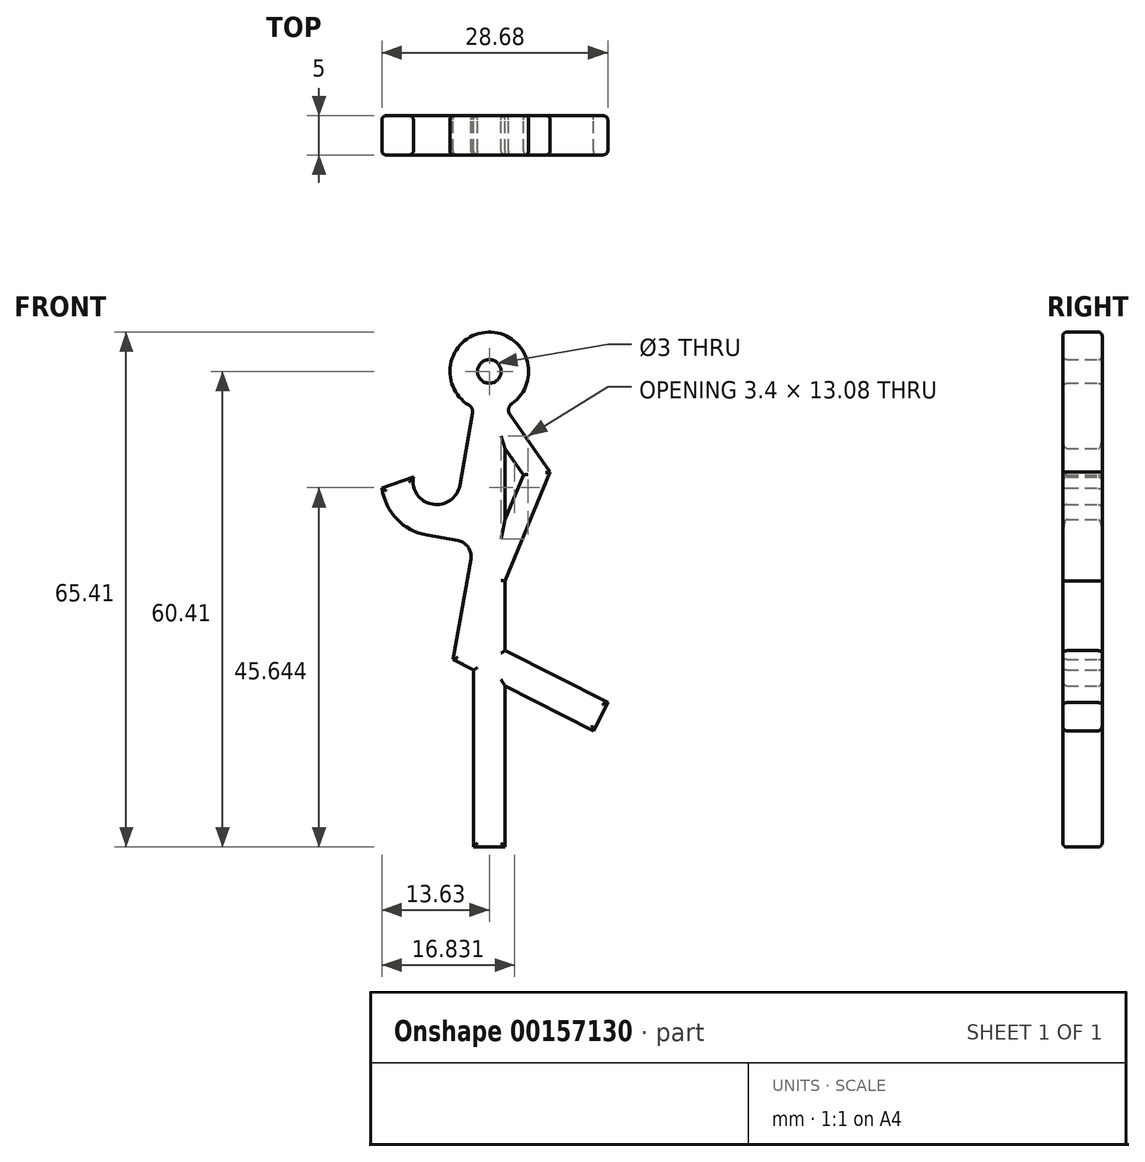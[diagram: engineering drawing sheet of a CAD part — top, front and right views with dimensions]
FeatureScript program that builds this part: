
annotation { "Feature Type Name" : "Feature", "Feature Type Description" : "" }
export const myFeature = defineFeature(function(context is Context, id is Id, definition is map)
    precondition{}
    {
        {
            var Q0;
            Q0=qCreatedBy(makeId("Front.planeOp"),FACE);
            var sketch = newSketch(context, id + "F0", { "sketchPlane" : qUnion([Q0])});
            skCircle(sketch, "E0", {"center": v(0, 0) * mm, "radius": 1.5 * mm});
            skCircle(sketch, "E1", {"center": v(0, 0) * mm, "radius": 5 * mm});
            skLineSegment(sketch, "E2", {"start": v(2, -4.58) * mm, "end": v(2, -60.41) * mm});
            skLineSegment(sketch, "E3", {"start": v(2, -60.41) * mm, "end": v(-2, -60.41) * mm});
            skLineSegment(sketch, "E4", {"start": v(-2, -60.41) * mm, "end": v(-2, -4.58) * mm});
            skLineSegment(sketch, "E5", {"start": v(2, -4.58) * mm, "end": v(7.74, -12.77) * mm});
            skLineSegment(sketch, "E6", {"start": v(7.74, -12.77) * mm, "end": v(2, -26.63) * mm});
            skLineSegment(sketch, "E7.0", {"start": v(4.33, -13.15) * mm, "end": v(-0.77, -25.49) * mm});
            skLineSegment(sketch, "E7.1", {"start": v(-0.46, -6.3) * mm, "end": v(4.33, -13.15) * mm});
            skLineSegment(sketch, "E8", {"start": v(-2, -4.58) * mm, "end": v(-3.74, -14.43) * mm});
            skLineSegment(sketch, "E9.0", {"start": v(-2, -21.84) * mm, "end": v(-7.9, -20.8) * mm});
            skArc(sketch, "E10", {"start": v(-3.74, -14.43) * mm, "mid": v(-7.21, -16.86) * mm, "end": v(-9.65, -13.39) * mm});
            skArc(sketch, "E11.0", {"start": v(-7.9, -20.8) * mm, "mid": v(-12.42, -17.92) * mm, "end": v(-13.58, -12.7) * mm});
            skLineSegment(sketch, "E12", {"start": v(-9.65, -13.39) * mm, "end": v(-13.63, -14.84) * mm});
            skLineSegment(sketch, "E13", {"start": v(-2, -21.84) * mm, "end": v(-4.6, -36.62) * mm});
            skLineSegment(sketch, "E14", {"start": v(-4.6, -36.62) * mm, "end": v(13.24, -45.65) * mm});
            skLineSegment(sketch, "E15.0", {"start": v(-0.15, -34.39) * mm, "end": v(15.05, -42.08) * mm});
            skLineSegment(sketch, "E15.1", {"start": v(1.94, -22.54) * mm, "end": v(-0.15, -34.39) * mm});
            skLineSegment(sketch, "E16", {"start": v(15.05, -42.08) * mm, "end": v(13.24, -45.65) * mm});
            skSolve(sketch);
        }
        {
            var Q0;
            Q0=makeQuery(id+"F0.imprint","IMPRINT",FACE,{"disambiguationData":[TD([[makeQuery(id+"F0.imprint","IMPRINT",EDGE,{"derivedFrom":sQuery(id+"F0.wireOp",EDGE,"E0")}),-1.0]])]});
            var Q1;
            {var subQ1=sQuery(id+"F0.wireOp",EDGE,"E5");Q1=makeQuery(id+"F0.imprint","IMPRINT",FACE,{"disambiguationData":[TD([[makeQuery(id+"F0.imprint","IMPRINT",EDGE,{"derivedFrom":subQ1}),-1.0]])]});}
            var Q2;
            {var subQ0=sQuery(id+"F0.wireOp",EDGE,"E2");var subQ7=makeQuery(id+"F0.imprint","INTERSECT",VERTEX,{"derivedFrom":[subQ0,sQuery(id+"F0.wireOp",EDGE,"E7.1")]});Q2=makeQuery(id+"F0.imprint","IMPRINT",FACE,{"disambiguationData":[TD([[makeQuery(id+"F0.imprint","IMPRINT",EDGE,{"disambiguationData":[TD([[subQ7,-1.0]])],"derivedFrom":subQ0}),-1.0]])]});}
            var Q3;
            {var subQ1=sQuery(id+"F0.wireOp",EDGE,"E8");Q3=makeQuery(id+"F0.imprint","IMPRINT",FACE,{"disambiguationData":[TD([[makeQuery(id+"F0.imprint","IMPRINT",EDGE,{"derivedFrom":subQ1}),1.0]])]});}
            var Q4;
            {var subQ0=sQuery(id+"F0.wireOp",EDGE,"E13");Q4=makeQuery(id+"F0.imprint","IMPRINT",FACE,{"disambiguationData":[TD([[makeQuery(id+"F0.imprint","IMPRINT",EDGE,{"derivedFrom":subQ0}),1.0]])]});}
            var Q5;
            {var subQ5=sQuery(id+"F0.wireOp",EDGE,"E16");Q5=makeQuery(id+"F0.imprint","IMPRINT",FACE,{"disambiguationData":[TD([[makeQuery(id+"F0.imprint","IMPRINT",EDGE,{"derivedFrom":subQ5}),-1.0]])]});}
            var Q6;
            {var subQ0=sQuery(id+"F0.wireOp",EDGE,"E3");Q6=makeQuery(id+"F0.imprint","IMPRINT",FACE,{"disambiguationData":[TD([[makeQuery(id+"F0.imprint","IMPRINT",EDGE,{"derivedFrom":subQ0}),-1.0]])]});}
            extrude(context, id + "F1", {"entities" : qUnion([Q0, Q1, Q2, Q3, Q4, Q5, Q6]), "depth" : 5 * mm});
        }
        {
            var Q0;
            Q0=makeQuery(id+"F1.opExtrude","SWEPT_EDGE",EDGE,{"disambiguationData":[OSD([sQuery(id+"F0.wireOp",EDGE,"E4"),sQuery(id+"F0.wireOp",EDGE,"E9.0"),sQuery(id+"F0.wireOp",EDGE,"E13")])]});
            fillet(context, id + "F2", {"entities" : qUnion([Q0]), "radius" : 2 * mm, "tangentPropagation" : true, "allowEdgeOverflow" : false});
        }
        {
            var Q0;
            Q0=makeQuery(id+"F1.opExtrude","SWEPT_EDGE",EDGE,{"disambiguationData":[OSD([sQuery(id+"F0.wireOp",EDGE,"E1"),sQuery(id+"F0.wireOp",EDGE,"E4"),sQuery(id+"F0.wireOp",EDGE,"E8")])]});
            var Q1;
            Q1=makeQuery(id+"F1.opExtrude","SWEPT_EDGE",EDGE,{"disambiguationData":[OSD([sQuery(id+"F0.wireOp",EDGE,"E1"),sQuery(id+"F0.wireOp",EDGE,"E2"),sQuery(id+"F0.wireOp",EDGE,"E5")])]});
            fillet(context, id + "F3", {"entities" : qUnion([Q0, Q1]), "radius" : 1 * mm, "tangentPropagation" : true, "allowEdgeOverflow" : false});
        }
        {
            var Q0;
            Q0=makeQuery(id+"F1.opExtrude","CAP_FACE",FACE,{"disambiguationData":[OSD([sQuery(id+"F0.wireOp",EDGE,"E0"),sQuery(id+"F0.wireOp",EDGE,"E1"),sQuery(id+"F0.wireOp",EDGE,"E2"),sQuery(id+"F0.wireOp",EDGE,"E3"),sQuery(id+"F0.wireOp",EDGE,"E4"),sQuery(id+"F0.wireOp",EDGE,"E5"),sQuery(id+"F0.wireOp",EDGE,"E6"),sQuery(id+"F0.wireOp",EDGE,"E7.0"),sQuery(id+"F0.wireOp",EDGE,"E7.1"),sQuery(id+"F0.wireOp",EDGE,"E8"),sQuery(id+"F0.wireOp",EDGE,"E9.0"),sQuery(id+"F0.wireOp",EDGE,"E10"),sQuery(id+"F0.wireOp",EDGE,"E11.0"),sQuery(id+"F0.wireOp",EDGE,"E12"),sQuery(id+"F0.wireOp",EDGE,"E13"),sQuery(id+"F0.wireOp",EDGE,"E14"),sQuery(id+"F0.wireOp",EDGE,"E15.0"),sQuery(id+"F0.wireOp",EDGE,"E16")])],"isStart":false});
            var Q1;
            Q1=makeQuery(id+"F1.opExtrude","CAP_FACE",FACE,{"disambiguationData":[OSD([sQuery(id+"F0.wireOp",EDGE,"E0"),sQuery(id+"F0.wireOp",EDGE,"E1"),sQuery(id+"F0.wireOp",EDGE,"E2"),sQuery(id+"F0.wireOp",EDGE,"E3"),sQuery(id+"F0.wireOp",EDGE,"E4"),sQuery(id+"F0.wireOp",EDGE,"E5"),sQuery(id+"F0.wireOp",EDGE,"E6"),sQuery(id+"F0.wireOp",EDGE,"E7.0"),sQuery(id+"F0.wireOp",EDGE,"E7.1"),sQuery(id+"F0.wireOp",EDGE,"E8"),sQuery(id+"F0.wireOp",EDGE,"E9.0"),sQuery(id+"F0.wireOp",EDGE,"E10"),sQuery(id+"F0.wireOp",EDGE,"E11.0"),sQuery(id+"F0.wireOp",EDGE,"E12"),sQuery(id+"F0.wireOp",EDGE,"E13"),sQuery(id+"F0.wireOp",EDGE,"E14"),sQuery(id+"F0.wireOp",EDGE,"E15.0"),sQuery(id+"F0.wireOp",EDGE,"E16")])],"isStart":true});
            fillet(context, id + "F4", {"entities" : qUnion([Q0, Q1]), "radius" : 0.5 * mm, "tangentPropagation" : true, "allowEdgeOverflow" : false});
        }
    });
